# Revit family: a_reynaers_cs-104-functional_door_inside-opening-brush_doublerfa
name_source: partatom
category: Окна
revit_build: Autodesk Revit 2017 (Build: 20160225_1515(x64)
units: mm (PartAtom-declared; Revit-internal decimal feet)

## family parameters
Всегда вертикально = Да
Заголовок OmniClass = Windows
Номер OmniClass = 23.30.20.00
Общий = Нет
Основа = Стена
При загрузке вырезать с полостями = Нет
Точка расчета площади = Нет

## types (1)
- Frame 82mm
    BE = Нет
    Date of publishing = 2015-09-17
    Default Sill Height = 0 мм
    Design country = Belgium
    Edition number = 1
    IFC Classification = Door
    Manufacturer country = Belgium
    Manufacturer name = Reynaers
    Material main = Aluminium
    Material secondary = Aluminium
    NBS Reference Code = 10-50-25-25
    NBS Reference Description = Doors, Windows And Glazing Survey Systems
    NL = Да
    Nominal height = 0
    Nominal width = 0
    Product Guid = 2fc0731a-14b4-4d12-820d-d65da8d0a27a
    Product SKU = Reynaers_door_Concept_system_104_HI
    Product data url = http://file-system.ru
    Product family = Windows & Doors
    Product group = Windows Aluminium
    QR code = http://file-system.ru
    REY Block Frame = Нет
    REY Brush Profile Height = 26 мм
    REY Built-In Depth = 95 мм
    REY Butt Strip Width = 25 мм
    REY Design = 0 мм
    REY Fixation Bottom = 33 мм
    REY Frame Position MID = 77 мм
    REY Frame Width = 82 мм
    REY Gap Floor = 7 мм
    REY Gap Width = 6 мм
    REY Joint Bottom = 0 мм
    REY Joint Width = 8 мм
    REY Joint Width A = 8 мм
    REY Joint Width B = 0 мм
    REY Offset Wall Ext Int = 25 мм
    REY Offset Wall Ext Int A = 25 мм
    REY Offset Wall Ext Int B = 0 мм
    REY Panel Coverage = 19 мм
    REY Profile Rebate = 25 мм
    REY Rebate = 30 мм
    REY Rebate A = 30 мм
    REY Rebate B = 0 мм
    REY Rebate TOP A = 30 мм
    REY Rebate TOP B = 0 мм
    REY Shutter = Нет
    REY Shutter Depth = 0 мм
    REY Shutter Height = 0 мм
    REY Shutter Position = 25 мм
    REY Shutter Roll Height = 200 мм
    REY Shutter Roll Material = <По категории>
    REY Sill H = 0 мм
    REY Sill Height = 0 мм
    REY Vent & Gap & 20 = 97 мм
    REY Vent Width = 71 мм
    REY Website = www.reynaers.com
    UNSPSC Code = 301715
    URL = http://www.reynaers.com
    Uniclass 1.4 Code = JL20
    Uniclass 1.4 Description = Doors
    Uniclass 2.0 Code = SS-10-50-25-25
    Uniclass 2.0 Description = Doors, Windows And Glazing Survey Systems
    Wall Exterior Width = 90 мм
    Weight Net (Kg) = 0
    Аналитическая конструкция = <None>
    Замыкание стены = По основе
    Изготовитель = Reynaers

## geometry (parser evidence)
native form markers: Sweep x6
no freeform markers — native parametric forms only
